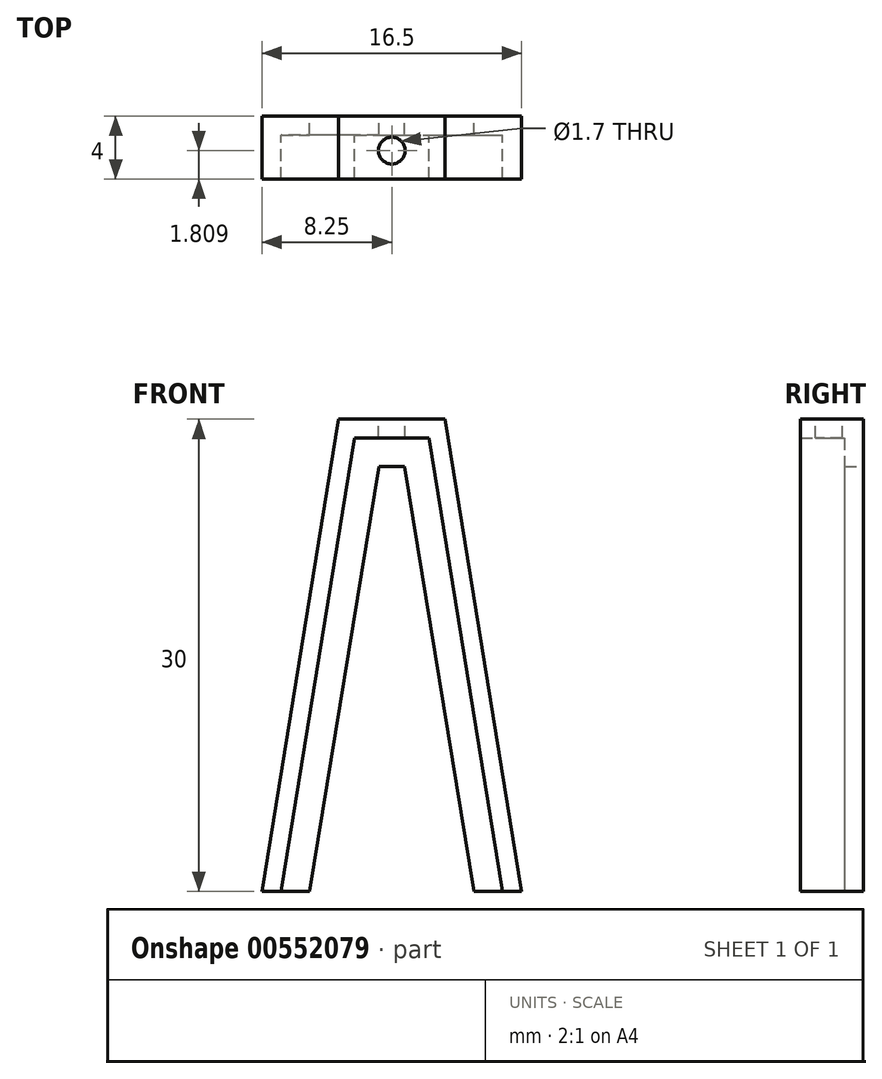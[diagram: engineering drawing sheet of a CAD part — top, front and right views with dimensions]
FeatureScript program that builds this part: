
annotation { "Feature Type Name" : "Feature", "Feature Type Description" : "" }
export const myFeature = defineFeature(function(context is Context, id is Id, definition is map)
    precondition{}
    {
        {
            var Q0;
            Q0=qCreatedBy(makeId("Front.planeOp"),FACE);
            var sketch = newSketch(context, id + "F0", { "sketchPlane" : qUnion([Q0])});
            skLineSegment(sketch, "E0", {"start": v(-3.38, 14.75) * mm, "end": v(3.38, 14.75) * mm});
            skLineSegment(sketch, "E1", {"start": v(-3.38, 14.75) * mm, "end": v(-8.25, -15.25) * mm});
            skLineSegment(sketch, "E2", {"start": v(3.38, 14.75) * mm, "end": v(8.25, -15.25) * mm});
            skLineSegment(sketch, "E3", {"start": v(-0.82, 11.75) * mm, "end": v(0.82, 11.75) * mm});
            skLineSegment(sketch, "E4", {"start": v(-2.35, 13.55) * mm, "end": v(2.35, 13.55) * mm});
            skLineSegment(sketch, "E5", {"start": v(0, 14.75) * mm, "end": v(0, 15.25) * mm});
            skLineSegment(sketch, "E6", {"start": v(-8.25, -15.25) * mm, "end": v(-5.21, -15.25) * mm});
            skLineSegment(sketch, "E7", {"start": v(5.21, -15.25) * mm, "end": v(8.25, -15.25) * mm});
            skLineSegment(sketch, "E8", {"start": v(0.82, 11.75) * mm, "end": v(5.21, -15.25) * mm});
            skLineSegment(sketch, "E9", {"start": v(2.35, 13.55) * mm, "end": v(7.03, -15.25) * mm});
            skLineSegment(sketch, "E10", {"start": v(-0.82, 11.75) * mm, "end": v(-5.21, -15.25) * mm});
            skLineSegment(sketch, "E11", {"start": v(-2.35, 13.55) * mm, "end": v(-7.03, -15.25) * mm});
            skSolve(sketch);
        }
        {
            var Q0;
            Q0=makeQuery(id+"F0.imprint","IMPRINT",FACE,{"disambiguationData":[TD([[makeQuery(id+"F0.imprint","IMPRINT",EDGE,{"derivedFrom":sQuery(id+"F0.wireOp",EDGE,"E3")}),1.0]])]});
            extrude(context, id + "F1", {"entities" : qUnion([Q0]), "depth" : 1.2 * mm, "offsetDistance" : 25 * mm});
        }
        {
            var Q0;
            {var subQ1=sQuery(id+"F0.wireOp",EDGE,"E1");Q0=makeQuery(id+"F0.imprint","IMPRINT",FACE,{"disambiguationData":[TD([[makeQuery(id+"F0.imprint","IMPRINT",EDGE,{"derivedFrom":subQ1}),1.0]])]});}
            extrude(context, id + "F2", {"entities" : qUnion([Q0]), "operationType" : NewBodyOperationType.ADD, "depth" : 4 * mm, "offsetDistance" : 25 * mm});
        }
        {
            var Q0;
            Q0=makeQuery(id+"F2.opExtrude","SWEPT_FACE",FACE,{"disambiguationData":[OSD([sQuery(id+"F0.wireOp",EDGE,"E0")])]});
            var sketch = newSketch(context, id + "F3", { "sketchPlane" : qUnion([Q0])});
            skCircle(sketch, "E12", {"center": v(0, -2.2) * mm, "radius": 0.85 * mm});
            skPoint(sketch, "E12.centerSnap0", {"position": v(0, 0) * mm});
            skSolve(sketch);
        }
        {
            var Q0;
            Q0=makeQuery(id+"F3.imprint","IMPRINT",FACE,{"disambiguationData":[TD([[makeQuery(id+"F3.imprint","IMPRINT",EDGE,{"derivedFrom":sQuery(id+"F3.wireOp",EDGE,"E12")}),1.0]])]});
            extrude(context, id + "F4", {"entities" : qUnion([Q0]), "operationType" : NewBodyOperationType.REMOVE, "oppositeDirection" : true, "depth" : 1.5 * mm, "offsetDistance" : 25 * mm});
        }
    });
